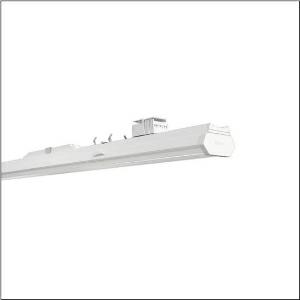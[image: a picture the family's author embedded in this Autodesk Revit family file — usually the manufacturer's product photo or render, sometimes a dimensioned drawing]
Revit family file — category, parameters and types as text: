
# Revit family: licross_21_protected_ho_52td11dn4dxs
name_source: partatom
category: Lighting Fixtures
units: mm (PartAtom-declared; Revit-internal decimal feet)

## family parameters
Cut with Voids When Loaded = No
Host = Face
Light Source = No
Part Type = Normal
Room Calculation Point = No
Round Connector Dimension = Use Diameter
Shared = No

## types (1)
- --- (1 x LED, 13000 lm, 73.1 W, 4000K)
    Apparent Load = 73 VA
    CIE Flux Codes = 84 94 98 99 100
    Color Rendering = 80
    Color Temperature = 4000K
    Default Elevation = 1800 mm
    Description = Licross 21 Protected HO, luminaire insert, of sheet steel, galvanised, coil coated, white, length: 1.500mm, width: 90mm, height: 103mm, LED rated luminous flux: 13.000lm, light colour: 840, SDCM (Standard Deviation of Colour Matching)MacAdam ≤ 3 SDCM (initial), control gear: DALI 2, with plug, 5-pole, with phase selection, mains connection: 220..240V, AC, 50/60Hz, rated input power: 73W, internal wiring halogen-free, primary light control with lens, of plastic, primary optical cover: cover, of PMMA, light emission: direct distribution, primary light characteristic: symmetric, protection rating (complete): IP54, insulation class (complete): insulation class I (protective earthing), certification: CE, ENEC, VDE, UKCA, protection symbol: D if used in an environment with non-conductive dust loads with corresponding accessories, impact resistance: IK06, permissible ambient temperature for indoor applications: -25..+40°C, corresponds to IFS (International Featured Standards) requirements for safety and quality in the food industry, reducing of maximum allowable ambient temperature of 5°C with ceiling mounting, LABS conformity tested according to VDMA 24364:2018-05, The light source and the operating device comply with the requirements of the Ecodesign Regulation (EU) 2019/2020 and are replaceable in accordance with this regulation, packaging unit: 1 piece
    Height = 92 mm
    Lamp = 1 x LED
    Lamp Light Flux = 13000 lm
    Lamp Power = 73.1 W
    Lamp count = 1
    Length = 1500 mm
    Luminous efficacy = 178 lm/W
    Manufacturer = Siteco
    ModVariant = No
    Model = 52TD11DN4DXS
    Mounting Place = Ceiling
    Mounting Type = Pendant
    Number of Poles = 1
    OnlyDefault = Yes
    Power Factor = 1
    Product Name = Licross 21 Protected HO
    Product group = luminaire insert | ceiling pendant
    ProductGroupID = 901
    Protection Class = Protection class I
    Protection Degree = IP 54
    RLX_Detail_Level = 1
    RLX_Emergency_Light_Flux = 0 lm
    RLX_Emergency_Type = 0
    RLX_Emergency_Type_DB = No
    RlxData = <blob elided: 24625 chars, md5=85c7641a>
    Socket = socket
    Standby Power = 0 W
    System Light Flux = 13000 lm
    System Power = 73 W
    Type Comments = factory setting: luminous flux: 100 % | dim-lin: 254 | 417 mA
    Type Image = l_1256148.jpg
    URL = http://relux.com
    VarID = @adj_128633
    Voltage = 0 V
    Weight = 0.00 kg
    Width = 88 mm

## geometry (parser evidence)
native form markers: Blend x4, Sweep x10
no freeform markers — native parametric forms only
